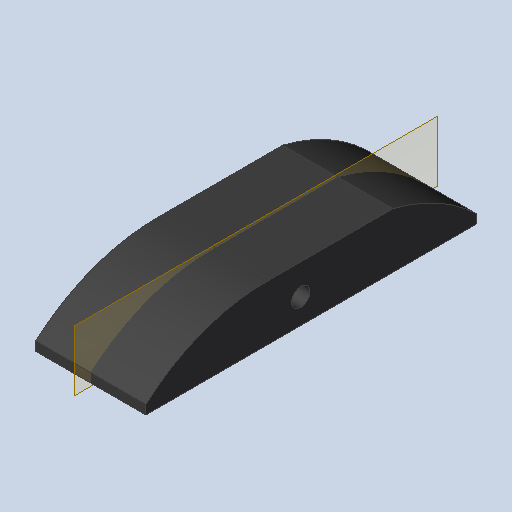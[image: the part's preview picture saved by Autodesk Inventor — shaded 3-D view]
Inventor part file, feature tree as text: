
AUTODESK INVENTOR PART (.ipt)
format: ipt  version: 2025.2 (Build 292293000, 293)  size: 134,144 bytes
history: native  units: in
note: dims shown in document units (in); Inventor stores cm internally (conversion verified against a paired STEP export)
features: sketch x5, extrude x4, other x3, plane x1, reference x1
ambient origin geometry x8: Origin, YZ Plane, XZ Plane, XY Plane, X Axis, Y Axis, Z Axis, Center Point
bodies: Solid1 (feature_tree)
feature tree (14):
  extrude  "Extrusion1"  Depth=3.0in
  extrude  "Extrusion2"  Depth=0.5in
  plane  "Work Plane1"
  extrude  "Extrusion4"  Depth=0.5in
  extrude  "Extrusion5"  Depth=3.0in
  sketch  "Sketch1"  dims[d0=13.0in d1=3.0in]
  sketch  "Sketch3"  dims[d5=3.0in d6=0.5in]
  sketch  "Sketch Rectangular Pattern1"  dims[d2=2.0in d3=0.5in]
  sketch  "Sketch5"  dims[d9=6.0in d10=3.0in]
  reference  "Reference1"
  sketch  "Sketch6"  dims[d11=6.0in d12=6.0in d13=0.0in d14=0.236in d15=0.25in d16=3.0in d17=0.7874in d19=5.5in d20=1.1811in d22=6.0in d25=0.5in d26=0.0in d37=10.0in d38=10.0in d39=0.0in d40=0.0in d41=1.0in d42=0.0in d43=0.0in]
  other  "<userpath>\Downloads\UAV_v0.2.0\UAV_v0.2.0\UAV_Assembly.iam"
  other  "UAV_Assembly.iam"
  other  "MiddleWingL_MIR:1"
